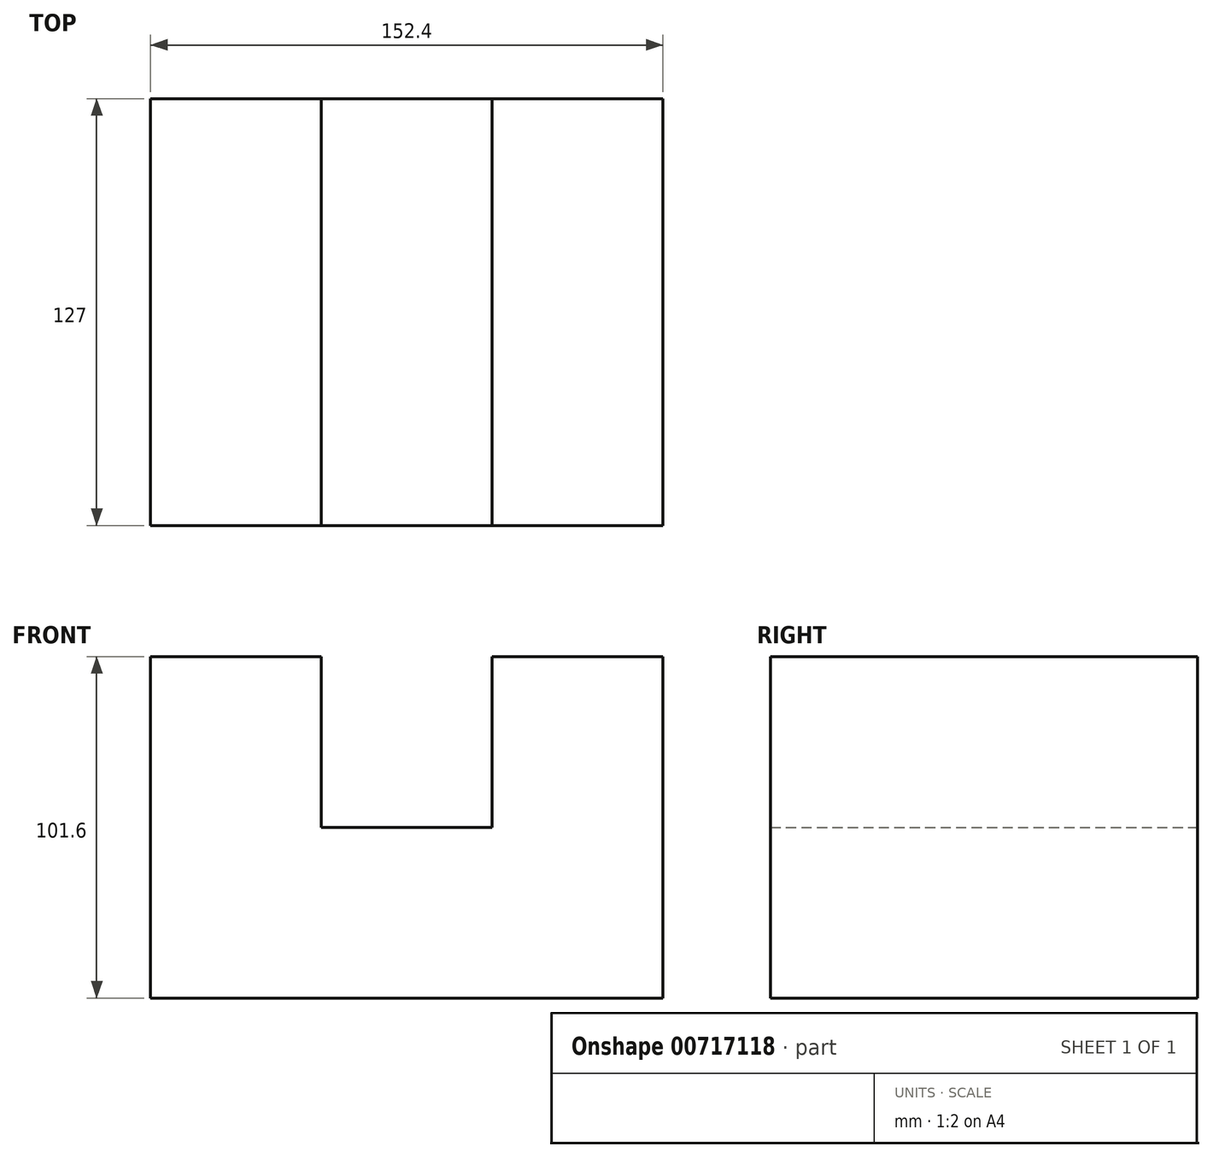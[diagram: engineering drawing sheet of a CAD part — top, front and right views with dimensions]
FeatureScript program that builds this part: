
annotation { "Feature Type Name" : "Feature", "Feature Type Description" : "" }
export const myFeature = defineFeature(function(context is Context, id is Id, definition is map)
    precondition{}
    {
        {
            var Q0;
            Q0=qCreatedBy(makeId("Front.planeOp"),FACE);
            var sketch = newSketch(context, id + "F0", { "sketchPlane" : qUnion([Q0])});
            skLineSegment(sketch, "E0", {"start": v(-64.9, 30.39) * mm, "end": v(-14.1, 30.39) * mm});
            skLineSegment(sketch, "E1", {"start": v(-14.1, 30.39) * mm, "end": v(-14.1, -20.41) * mm});
            skLineSegment(sketch, "E2", {"start": v(-14.1, -20.41) * mm, "end": v(36.7, -20.41) * mm});
            skLineSegment(sketch, "E3", {"start": v(36.7, -20.41) * mm, "end": v(36.7, 30.39) * mm});
            skLineSegment(sketch, "E4", {"start": v(36.7, 30.39) * mm, "end": v(87.5, 30.39) * mm});
            skLineSegment(sketch, "E5", {"start": v(87.5, 30.39) * mm, "end": v(87.5, -71.21) * mm});
            skLineSegment(sketch, "E6", {"start": v(87.5, -71.21) * mm, "end": v(-64.9, -71.21) * mm});
            skLineSegment(sketch, "E7", {"start": v(-64.9, -71.21) * mm, "end": v(-64.9, 30.39) * mm});
            skSolve(sketch);
        }
        {
            var Q0;
            Q0=makeQuery(id+"F0.imprint","IMPRINT",FACE,{"disambiguationData":[TD([[makeQuery(id+"F0.imprint","IMPRINT",EDGE,{"derivedFrom":sQuery(id+"F0.wireOp",EDGE,"E0")}),-1.0]])]});
            extrude(context, id + "F1", {"entities" : qUnion([Q0]), "depth" : 127 * mm, "offsetDistance" : 25.4 * mm});
        }
    });
